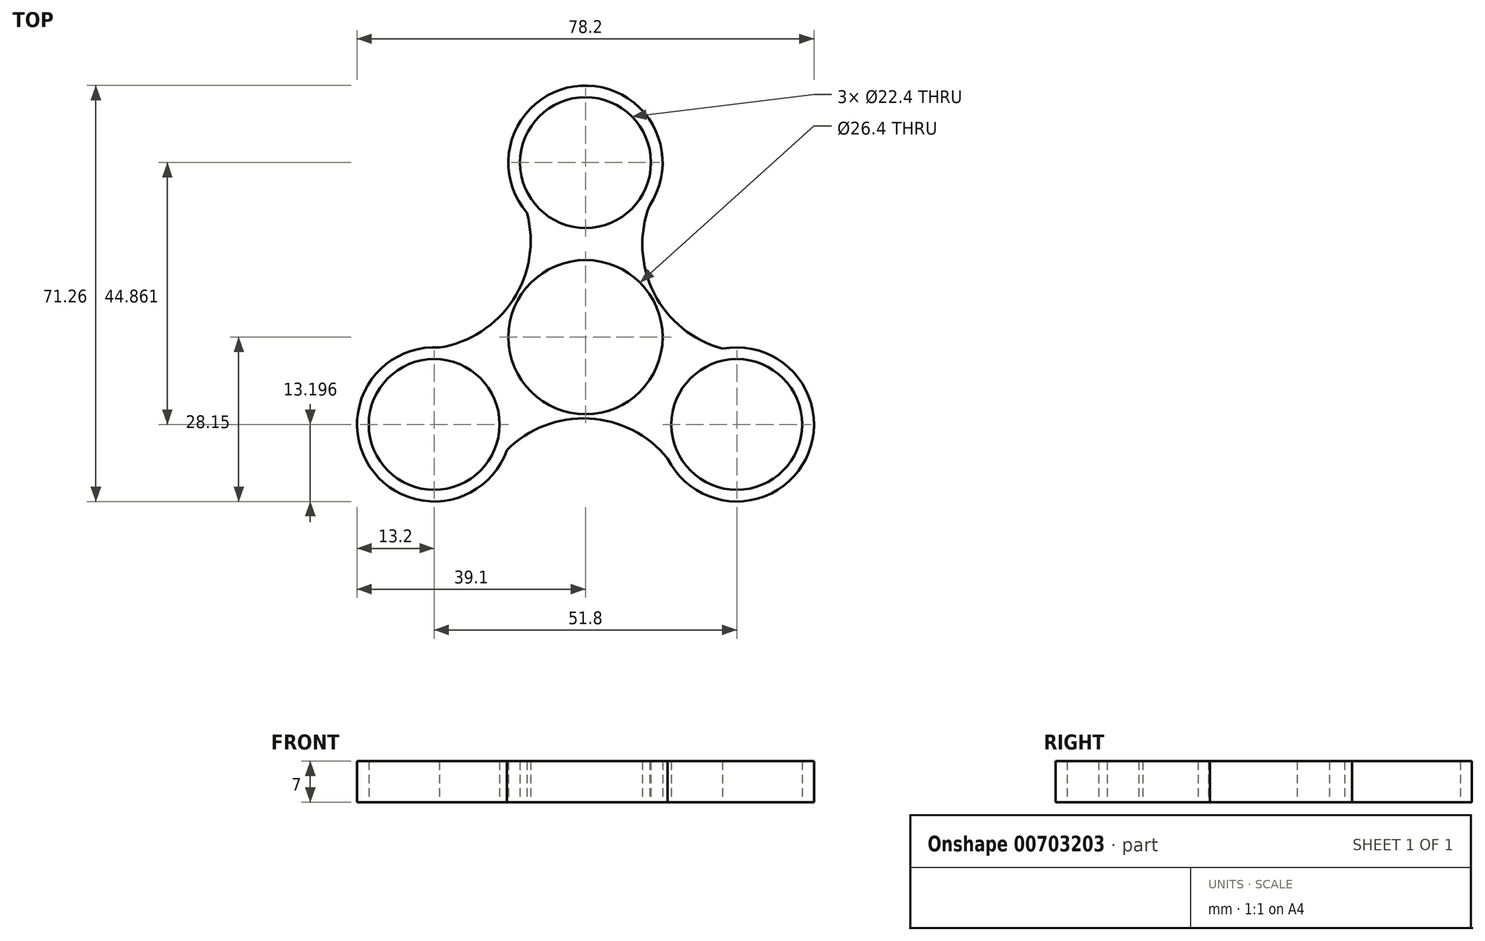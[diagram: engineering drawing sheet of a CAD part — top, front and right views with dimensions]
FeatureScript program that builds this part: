
annotation { "Feature Type Name" : "Feature", "Feature Type Description" : "" }
export const myFeature = defineFeature(function(context is Context, id is Id, definition is map)
    precondition{}
    {
        {
            var Q0;
            Q0=qCreatedBy(makeId("Top.planeOp"),FACE);
            var sketch = newSketch(context, id + "F0", { "sketchPlane" : qUnion([Q0])});
            skCircle(sketch, "E0", {"center": v(0, 0) * mm, "radius": 11.2 * mm});
            skCircle(sketch, "E1", {"center": v(0, 0) * mm, "radius": 13.2 * mm});
            skCircle(sketch, "E2", {"center": v(0, 29.9) * mm, "radius": 11.2 * mm});
            skCircle(sketch, "E3", {"center": v(0, 29.9) * mm, "radius": 13.2 * mm});
            skCircle(sketch, "E4.1.0", {"center": v(-25.9, -14.95) * mm, "radius": 13.2 * mm});
            skCircle(sketch, "E4.1.1", {"center": v(-25.9, -14.95) * mm, "radius": 11.2 * mm});
            skCircle(sketch, "E4.2.0", {"center": v(25.9, -14.95) * mm, "radius": 13.2 * mm});
            skCircle(sketch, "E4.2.1", {"center": v(25.9, -14.95) * mm, "radius": 11.2 * mm});
            skArc(sketch, "E5", {"start": v(10.97, 22.57) * mm, "mid": v(11.75, 7.5) * mm, "end": v(23.47, -1.98) * mm});
            skArc(sketch, "E6.1.0", {"start": v(-25.03, -1.78) * mm, "mid": v(-12.38, 6.42) * mm, "end": v(-10.02, 21.31) * mm});
            skArc(sketch, "E6.2.0", {"start": v(14.06, -20.79) * mm, "mid": v(0.63, -13.93) * mm, "end": v(-13.45, -19.33) * mm});
            skSolve(sketch);
        }
        {
            var Q0;
            Q0 = qSketchRegion(id + "F0", true);
            extrude(context, id + "F1", {"entities" : qUnion([Q0]), "depth" : 7 * mm, "offsetDistance" : 25 * mm});
        }
    });
